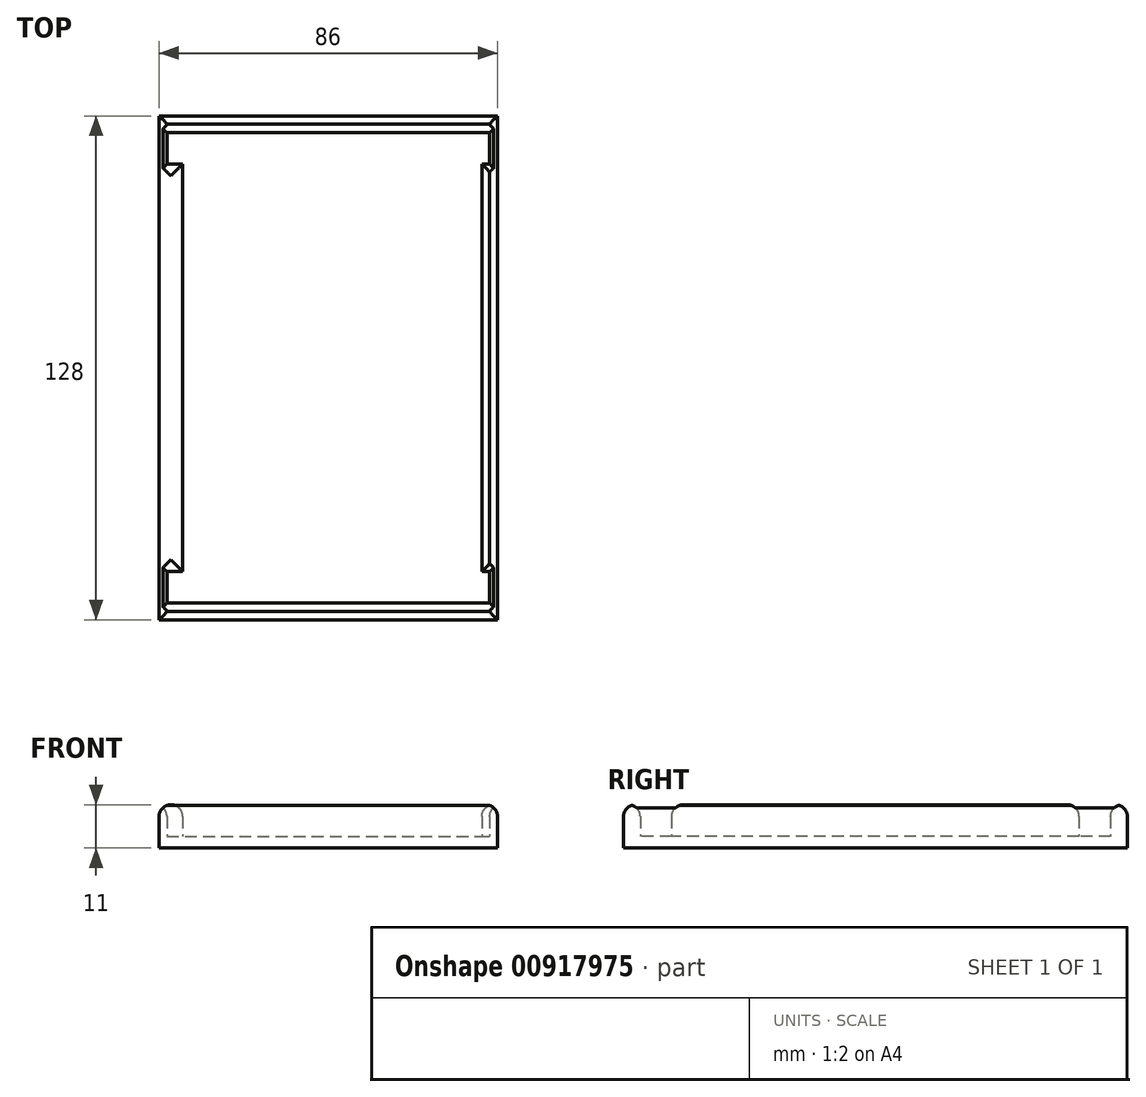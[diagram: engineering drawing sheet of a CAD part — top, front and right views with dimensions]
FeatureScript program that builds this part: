
annotation { "Feature Type Name" : "Feature", "Feature Type Description" : "" }
export const myFeature = defineFeature(function(context is Context, id is Id, definition is map)
    precondition{}
    {
        {
            var Q0;
            Q0=qCreatedBy(makeId("Top.planeOp"),FACE);
            var sketch = newSketch(context, id + "F0", { "sketchPlane" : qUnion([Q0])});
            skLineSegment(sketch, "E0.bottom", {"start": v(-43, -64) * mm, "end": v(43, -64) * mm});
            skLineSegment(sketch, "E0.top", {"start": v(-43, 64) * mm, "end": v(43, 64) * mm});
            skLineSegment(sketch, "E0.left", {"start": v(-43, -64) * mm, "end": v(-43, 64) * mm});
            skLineSegment(sketch, "E0.right", {"start": v(43, -64) * mm, "end": v(43, 64) * mm});
            skLineSegment(sketch, "E1", {"start": v(0, 64) * mm, "end": v(0, 0) * mm, "construction": true});
            skLineSegment(sketch, "E2", {"start": v(0, -64) * mm, "end": v(0, 0) * mm, "construction": true});
            skLineSegment(sketch, "E3", {"start": v(-43, 0) * mm, "end": v(0, 0) * mm, "construction": true});
            skLineSegment(sketch, "E4", {"start": v(43, 0) * mm, "end": v(0, 0) * mm, "construction": true});
            skSolve(sketch);
        }
        {
            var Q0;
            Q0=makeQuery(id+"F0.imprint","IMPRINT",FACE,{"disambiguationData":[TD([[makeQuery(id+"F0.imprint","IMPRINT",EDGE,{"derivedFrom":sQuery(id+"F0.wireOp",EDGE,"E0.bottom")}),1.0]])]});
            var sketch = newSketch(context, id + "F1", { "sketchPlane" : qUnion([Q0])});
            skPoint(sketch, "E5", {"position": v(-43, 64) * mm});
            skPoint(sketch, "E6", {"position": v(43, 64) * mm});
            skPoint(sketch, "E7", {"position": v(43, -64) * mm});
            skPoint(sketch, "E8", {"position": v(-43, -64) * mm});
            skPoint(sketch, "E9", {"position": v(0, 0) * mm});
            skLineSegment(sketch, "E10.bottom", {"start": v(-43, 64) * mm, "end": v(43, 64) * mm});
            skLineSegment(sketch, "E10.top", {"start": v(-43, -64) * mm, "end": v(43, -64) * mm});
            skLineSegment(sketch, "E10.left", {"start": v(-43, 64) * mm, "end": v(-43, -64) * mm});
            skLineSegment(sketch, "E10.right", {"start": v(43, 64) * mm, "end": v(43, -64) * mm});
            skLineSegment(sketch, "E11", {"start": v(0, 64) * mm, "end": v(0, 59.75) * mm, "construction": true});
            skLineSegment(sketch, "E12", {"start": v(41, 0) * mm, "end": v(39, 0) * mm, "construction": true});
            skLineSegment(sketch, "E13", {"start": v(0, -64) * mm, "end": v(0, -59.75) * mm, "construction": true});
            skPoint(sketch, "E14", {"position": v(0, 59.75) * mm});
            skPoint(sketch, "E15", {"position": v(0, -59.75) * mm});
            skLineSegment(sketch, "E16", {"start": v(-43, -59.75) * mm, "end": v(-41, -59.75) * mm, "construction": true});
            skLineSegment(sketch, "E17", {"start": v(-43, 59.75) * mm, "end": v(-41, 59.75) * mm, "construction": true});
            skLineSegment(sketch, "E18", {"start": v(-41, 64) * mm, "end": v(-41, 59.75) * mm, "construction": true});
            skLineSegment(sketch, "E19", {"start": v(41, 64) * mm, "end": v(41, 59.75) * mm, "construction": true});
            skPoint(sketch, "E20", {"position": v(-41, 59.75) * mm});
            skPoint(sketch, "E21", {"position": v(41, 59.75) * mm});
            skPoint(sketch, "E22", {"position": v(-41, -59.75) * mm});
            skPoint(sketch, "E23", {"position": v(41, -59.75) * mm});
            skLineSegment(sketch, "E24.trimOffspring", {"start": v(-41, -59.75) * mm, "end": v(-41, -64) * mm, "construction": true});
            skLineSegment(sketch, "E25.trimOffspring", {"start": v(41, -59.75) * mm, "end": v(41, -64) * mm, "construction": true});
            skLineSegment(sketch, "E26.trimOffspring", {"start": v(41, 59.75) * mm, "end": v(43, 59.75) * mm, "construction": true});
            skLineSegment(sketch, "E27.trimOffspring", {"start": v(41, -59.75) * mm, "end": v(43, -59.75) * mm, "construction": true});
            skLineSegment(sketch, "E28.bottom", {"start": v(-41, 59.75) * mm, "end": v(41, 59.75) * mm});
            skLineSegment(sketch, "E28.top", {"start": v(-41, -59.75) * mm, "end": v(41, -59.75) * mm});
            skLineSegment(sketch, "E28.left", {"start": v(-41, 59.75) * mm, "end": v(-41, 51.75) * mm});
            skLineSegment(sketch, "E28.right", {"start": v(41, 59.75) * mm, "end": v(41, 51.75) * mm});
            skPoint(sketch, "E29", {"position": v(39, 0) * mm});
            skPoint(sketch, "E30", {"position": v(-41, 51.75) * mm});
            skPoint(sketch, "E31", {"position": v(-41, -51.75) * mm});
            skPoint(sketch, "E32", {"position": v(41, 51.75) * mm});
            skPoint(sketch, "E33", {"position": v(41, -51.75) * mm});
            skPoint(sketch, "E34", {"position": v(-37, 51.75) * mm});
            skLineSegment(sketch, "E35", {"start": v(-37, 51.75) * mm, "end": v(-37, -51.75) * mm});
            skPoint(sketch, "E36", {"position": v(-37, -51.75) * mm});
            skLineSegment(sketch, "E37", {"start": v(-41, 51.75) * mm, "end": v(-37, 51.75) * mm});
            skLineSegment(sketch, "E38", {"start": v(-41, -51.75) * mm, "end": v(-37, -51.75) * mm});
            skLineSegment(sketch, "E39.trimOffspring", {"start": v(-41, -51.75) * mm, "end": v(-41, -59.75) * mm});
            skLineSegment(sketch, "E40.trimOffspring", {"start": v(41, -51.75) * mm, "end": v(41, -59.75) * mm});
            skPoint(sketch, "E41.start.orphan", {"position": v(-43, 0) * mm});
            skPoint(sketch, "E42.orphan", {"position": v(43, 0) * mm});
            skPoint(sketch, "E43", {"position": v(-37, 0) * mm});
            skPoint(sketch, "E44", {"position": v(39, 51.75) * mm});
            skPoint(sketch, "E45", {"position": v(39, -51.75) * mm});
            skLineSegment(sketch, "E46", {"start": v(39, 51.75) * mm, "end": v(39, -51.75) * mm});
            skLineSegment(sketch, "E47", {"start": v(39, 51.75) * mm, "end": v(41, 51.75) * mm});
            skLineSegment(sketch, "E48", {"start": v(39, -51.75) * mm, "end": v(41, -51.75) * mm});
            skLineSegment(sketch, "E49", {"start": v(-43, 0) * mm, "end": v(43, 0) * mm, "construction": true});
            skSolve(sketch);
        }
        {
            var Q0;
            Q0 = qSketchRegion(id + "F1", true);
            extrude(context, id + "F2", {"entities" : qUnion([Q0]), "depth" : 8 * mm, "offsetDistance" : 25 * mm});
        }
        {
            var Q0;
            Q0 = qSketchRegion(id + "F0", true);
            extrude(context, id + "F3", {"entities" : qUnion([Q0]), "operationType" : NewBodyOperationType.ADD, "oppositeDirection" : true, "depth" : 3 * mm, "offsetDistance" : 25 * mm});
        }
        {
            var Q0;
            Q0=makeQuery(id+"F2.opExtrude","CAP_EDGE",EDGE,{"disambiguationData":[OSD([sQuery(id+"F1.wireOp",EDGE,"E35")])],"isStart":false});
            var Q1;
            Q1=makeQuery(id+"F2.opExtrude","CAP_FACE",FACE,{"disambiguationData":[OSD([sQuery(id+"F1.wireOp",EDGE,"E10.bottom"),sQuery(id+"F1.wireOp",EDGE,"E10.top"),sQuery(id+"F1.wireOp",EDGE,"E10.left"),sQuery(id+"F1.wireOp",EDGE,"E10.right"),sQuery(id+"F1.wireOp",EDGE,"E28.bottom"),sQuery(id+"F1.wireOp",EDGE,"E28.top"),sQuery(id+"F1.wireOp",EDGE,"E28.left"),sQuery(id+"F1.wireOp",EDGE,"E28.right"),sQuery(id+"F1.wireOp",EDGE,"E35"),sQuery(id+"F1.wireOp",EDGE,"E37"),sQuery(id+"F1.wireOp",EDGE,"E38"),sQuery(id+"F1.wireOp",EDGE,"E39.trimOffspring"),sQuery(id+"F1.wireOp",EDGE,"TgZsBDhP-Z1rQ-D3Fd-dSFC-g1RpR0Ooo2CT"),sQuery(id+"F1.wireOp",EDGE,"o2WYqlwp-1E9i-5UEq-BMk1-qadRsqGrwnMw"),sQuery(id+"F1.wireOp",EDGE,"v0YyFTxK-eSxl-pMVM-Frwt-2nECoXs77DLj"),sQuery(id+"F1.wireOp",EDGE,"E40.trimOffspring")])],"isStart":false});
            fillet(context, id + "F4", {"entities" : qUnion([Q0, Q1]), "radius" : 3 * mm, "tangentPropagation" : true, "allowEdgeOverflow" : false});
        }
    });
